# Revit family: TR2073
name_source: partatom
category: Verbindungsmittel
units: mm (PartAtom-declared; Revit-internal decimal feet)

## family parameters
Arbeitsebenenbasiert = Nein
Beim Laden mit Abzugskörper schneiden = Nein
Gemeinsam genutzt = Nein
Immer vertikal = Nein
OmniClass-Nummer = 23.25.10.27.11.21
OmniClass-Titel = Reinforcement Couplers

## types (10) — shared parameters
Endenbearbeitung 1 = Mit Gewinde
Endenbearbeitung 2 = Mit Gewinde
Hersteller = Stahlwerk Annahütte Max Aicher GmbH Co.KG
Modell = TR 2073
Stabgröße 2 = Keine
TR2073-G_Vis = Ja
TR2073-L_Vis = Ja
TR2073-SW_Vis = Ja
Typenbild = TR2073.png
URL = http//:www.annahuette.com
zero-valued in all types: Einfassung Stab 2

## per-type parameters (varying)
| type | Außendurchmesser | Beschreibung | Einfassung Stab 1 | Gesamtlänge | Körper | Stabgröße 1 | TR2073-G | TR2073-L | TR2073-L1 | TR2073-Ld | TR2073-SW | TR2073-ø | TR2073-ød | Typenkommentare |
| TR 2073-ø18 | 32 mm  [stored 0.104987 ft] | TR2073-ø18 | 35 mm  [stored 0.114829 ft] | 35 mm  [stored 0.114829 ft] | 0,28 kg | SAS 670 - ø18 | 0,28 kg | 35 mm  [stored 0.114829 ft] | 15 mm  [stored 0.0492126 ft] | 20 mm  [stored 0.0656168 ft] | 32 mm  [stored 0.104987 ft] | 55 mm  [stored 0.180446 ft] | 18 mm  [stored 0.0590551 ft] | TR 2073 - Ankerstück |
| TR 2073-ø22 | 36 mm  [stored 0.11811 ft] | TR2073-ø22 | 45 mm  [stored 0.147638 ft] | 45 mm  [stored 0.147638 ft] | 0,43 kg | SAS 670 - ø22 | 0,43 kg | 45 mm  [stored 0.147638 ft] | 25 mm  [stored 0.082021 ft] | 20 mm  [stored 0.0656168 ft] | 36 mm  [stored 0.11811 ft] | 65 mm  [stored 0.213255 ft] | 22 mm  [stored 0.0721785 ft] | TR 2073 - Ankermutter mit Bund |
| TR 2073-ø25 | 41 mm  [stored 0.134514 ft] | TR2073-ø25 | 50 mm  [stored 0.164042 ft] | 50 mm  [stored 0.164042 ft] | 0,62 kg | SAS 670 - ø25 | 0,62 kg | 50 mm  [stored 0.164042 ft] | 30 mm  [stored 0.0984252 ft] | 20 mm  [stored 0.0656168 ft] | 41 mm  [stored 0.134514 ft] | 75 mm | 25 mm  [stored 0.082021 ft] | TR 2073 - Ankermutter mit Bund |
| TR 2073-ø28 | 46 mm  [stored 0.150919 ft] | TR2073-ø28 | 55 mm  [stored 0.180446 ft] | 55 mm  [stored 0.180446 ft] | 0,85 kg | SAS 670 - ø28 | 0,85 kg | 55 mm  [stored 0.180446 ft] | 35 mm  [stored 0.114829 ft] | 20 mm  [stored 0.0656168 ft] | 46 mm  [stored 0.150919 ft] | 85 mm  [stored 0.278871 ft] | 28 mm  [stored 0.0918635 ft] | TR 2073 - Ankerstück |
| TR 2073-ø30 | 50 mm  [stored 0.164042 ft] | TR2073-ø30 | 60 mm  [stored 0.19685 ft] | 60 mm  [stored 0.19685 ft] | 1,03 kg | SAS 670 - ø30 | 1,03 kg | 60 mm  [stored 0.19685 ft] | 40 mm  [stored 0.131234 ft] | 20 mm  [stored 0.0656168 ft] | 50 mm  [stored 0.164042 ft] | 90 mm  [stored 0.295276 ft] | 30 mm  [stored 0.0984252 ft] | TR 2073 - Ankermutter mit Bund |
| TR 2073-ø35 | 60 mm  [stored 0.19685 ft] | TR2073-ø35 | 70 mm  [stored 0.229659 ft] | 70 mm  [stored 0.229659 ft] | 1,66 kg | SAS 670 - ø35 | 1,66 kg | 70 mm  [stored 0.229659 ft] | 40 mm  [stored 0.131234 ft] | 30 mm  [stored 0.0984252 ft] | 60 mm  [stored 0.19685 ft] | 105 mm  [stored 0.344488 ft] | 35 mm  [stored 0.114829 ft] | TR 2073 - Ankermutter mit Bund |
| TR 2073-ø43 | 70 mm  [stored 0.229659 ft] | TR2073-ø43 | 85 mm  [stored 0.278871 ft] | 85 mm  [stored 0.278871 ft] | 2,74 kg | SAS 670 - ø43 | 2,74 kg | 85 mm  [stored 0.278871 ft] | 55 mm  [stored 0.180446 ft] | 30 mm  [stored 0.0984252 ft] | 70 mm  [stored 0.229659 ft] | 130 mm  [stored 0.426509 ft] | 43 mm  [stored 0.141076 ft] | TR 2073 - Ankermutter mit Bund |
| TR 2073-ø50 | 80 mm  [stored 0.262467 ft] | TR2073-ø50 | 100 mm  [stored 0.328084 ft] | 100 mm  [stored 0.328084 ft] | 3,63 kg | SAS 670 - ø50 | 3,63 kg | 100 mm  [stored 0.328084 ft] | 70 mm  [stored 0.229659 ft] | 30 mm  [stored 0.0984252 ft] | 80 mm  [stored 0.262467 ft] | 150 mm | 50 mm  [stored 0.164042 ft] | TR 2073 - Ankermutter mit Bund |
| TR 2073-ø57,5 | 90 mm  [stored 0.295276 ft] | TR2073-ø57,5 | 115 mm  [stored 0.377297 ft] | 115 mm  [stored 0.377297 ft] | 6,96 kg | SAS 670 - ø57,5 | 6,96 kg | 115 mm  [stored 0.377297 ft] | 85 mm  [stored 0.278871 ft] | 30 mm  [stored 0.0984252 ft] | 90 mm  [stored 0.295276 ft] | 175 mm  [stored 0.574147 ft] | 58 mm | TR 2073 - Ankermutter mit Bund |
| TR 2073-ø63,5 | 100 mm  [stored 0.328084 ft] | TR2073-ø63,5 | 125 mm  [stored 0.410105 ft] | 125 mm  [stored 0.410105 ft] | 8,78 kg | SAS 670 - ø63,5 | 8,78 kg | 125 mm  [stored 0.410105 ft] | 85 mm  [stored 0.278871 ft] | 40 mm  [stored 0.131234 ft] | 100 mm  [stored 0.328084 ft] | 190 mm | 64 mm | TR 2073 - Ankermutter mit Bund |

note: [stored X ft] marks values corroborated as IEEE doubles in the binary element streams (Revit-internal decimal feet)
